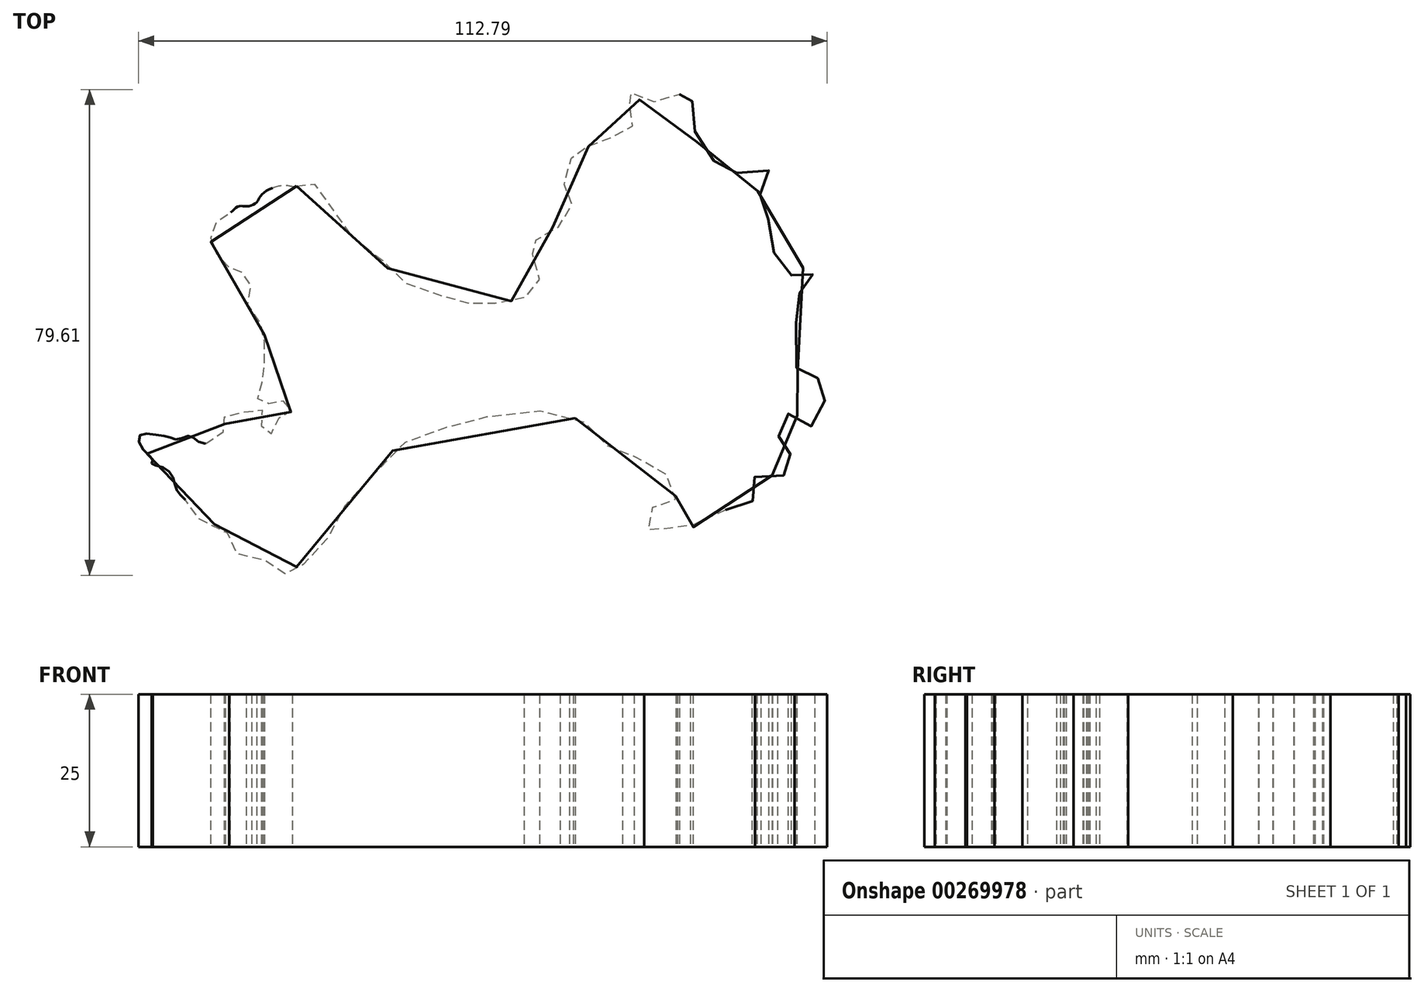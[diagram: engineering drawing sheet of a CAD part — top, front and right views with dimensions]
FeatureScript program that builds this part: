
annotation { "Feature Type Name" : "Feature", "Feature Type Description" : "" }
export const myFeature = defineFeature(function(context is Context, id is Id, definition is map)
    precondition{}
    {
        {
            var Q0;
            Q0=qCreatedBy(makeId("Top.planeOp"),FACE);
            var sketch = newSketch(context, id + "F0", { "sketchPlane" : qUnion([Q0])});
            skFitSpline(sketch, "E0", {"points": [v(-28.5, 30.47) * mm, v(-27.34, 31.77) * mm, v(-26.03, 31.34) * mm, v(-24.59, 29.31) * mm, v(-22.42, 26.42) * mm, v(-21.26, 23.82) * mm, v(-18.08, 21.36) * mm, v(-14.47, 18.33) * mm, v(-12.59, 15.72) * mm, v(-9.26, 14.13) * mm, v(-4.78, 12.54) * mm, v(-2.18, 11.38) * mm, v(0, 11.24) * mm, v(1.73, 10.52) * mm, v(4.33, 11.38) * mm, v(7.22, 11.67) * mm, v(9.68, 12.83) * mm, v(10.4, 14.28) * mm, v(11.27, 15.14) * mm, v(11.13, 16.88) * mm, v(10.4, 19.05) * mm, v(8.81, 21.36) * mm, v(10.55, 21.5) * mm, v(12.14, 23.53) * mm, v(14.45, 23.82) * mm, v(16.48, 25.55) * mm, v(16.62, 27.43) * mm, v(14.74, 29.46) * mm, v(15.18, 30.62) * mm, v(17.06, 32.06) * mm, v(16.33, 35.53) * mm, v(16.33, 36.4) * mm, v(18.65, 36.83) * mm, v(20.96, 37.41) * mm, v(22.84, 38.28) * mm, v(24.72, 39.44) * mm, v(26.3, 39.87) * mm, v(26.74, 41.75) * mm, v(26.74, 43.2) * mm, v(25.44, 44.79) * mm, v(25, 46.23) * mm, v(26.89, 45.36) * mm, v(28.62, 44.06) * mm, v(30.21, 44.35) * mm, v(32.67, 44.79) * mm, v(34.26, 45.5) * mm, v(33.97, 43.77) * mm, v(35.42, 43.77) * mm, v(36.43, 44.35) * mm, v(36, 41.75) * mm, v(36.58, 40.16) * mm, v(37.88, 35.39) * mm, v(39.47, 34.66) * mm, v(41.2, 33.94) * mm, v(42.8, 32.06) * mm, v(43.95, 32.93) * mm, v(46.26, 33.07) * mm, v(48.87, 33.07) * mm, v(47.7, 31.63) * mm, v(46.99, 29.9) * mm, v(47.57, 28.74) * mm, v(46.84, 27) * mm, v(48.43, 25.41) * mm, v(49.44, 23.24) * mm, v(49.44, 20.5) * mm, v(50.46, 18.18) * mm, v(51.47, 16.73) * mm, v(52.63, 15.87) * mm, v(54.36, 17.02) * mm, v(55.52, 17.02) * mm, v(56.24, 15.58) * mm, v(56.39, 14.57) * mm, v(55.23, 13.84) * mm, v(53.35, 12.25) * mm, v(53.06, 10.23) * mm, v(53.35, 8.06) * mm, v(53.5, 5.02) * mm, v(53.78, 0) * mm, v(54.94, 0) * mm, v(55.23, 0) * mm, v(56.96, -1.05) * mm, v(57.83, -1.34) * mm, v(58.4, -2.79) * mm, v(57.98, -5.1) * mm, v(57.69, -6.7) * mm, v(56.24, -8.86) * mm, v(54.8, -8.28) * mm, v(54.07, -7.41) * mm, v(52.2, -6.83) * mm, v(51.04, -7.41) * mm, v(50.31, -9.3) * mm, v(50.6, -10.74) * mm, v(51.32, -11.46) * mm, v(52.2, -11.9) * mm, v(52.48, -13.34) * mm, v(52.05, -14.35) * mm, v(53.06, -14.93) * mm, v(50.6, -17.25) * mm, v(48.58, -16.52) * mm, v(46.84, -16.96) * mm, v(46.12, -18.11) * mm, v(46.55, -19.41) * mm, v(46.4, -20.86) * mm, v(44.96, -21.87) * mm, v(43.08, -21.73) * mm, v(40.91, -23.17) * mm, v(36.86, -24.33) * mm, v(36.29, -26.21) * mm, v(34.12, -25.92) * mm, v(31.23, -25.78) * mm, v(30.07, -26.64) * mm, v(28.77, -25.05) * mm, v(28.62, -23.17) * mm, v(30.07, -22.16) * mm, v(32.24, -22.3) * mm, v(33.54, -21) * mm, v(33.54, -19.85) * mm, v(32.53, -17.54) * mm, v(30.94, -15.66) * mm, v(27.32, -14.06) * mm, v(24.43, -12.76) * mm, v(22.55, -12.18) * mm, v(21.1, -10.02) * mm, v(17.78, -7.85) * mm, v(12, -6.4) * mm, v(3.32, -7.41) * mm, v(0, -7.41) * mm, v(-6.51, -10.3) * mm, v(-10.85, -11.6) * mm, v(-15.2, -15.66) * mm, v(-17.5, -19.41) * mm, v(-21.7, -22.89) * mm, v(-22.7, -25.34) * mm, v(-25.75, -31.27) * mm, v(-27.48, -31.56) * mm, v(-28.2, -31.56) * mm, v(-29.5, -33.3) * mm, v(-31.24, -32.43) * mm, v(-32.4, -31.85) * mm, v(-33.55, -30.98) * mm, v(-36.01, -29.68) * mm, v(-38.18, -29.83) * mm, v(-39.48, -28.52) * mm, v(-39.48, -26.93) * mm, v(-40.93, -25.63) * mm, v(-43.82, -24.19) * mm, v(-45.56, -23.75) * mm, v(-45.99, -22.02) * mm, v(-47.44, -20.28) * mm, v(-48.3, -18.98) * mm, v(-48.88, -16.96) * mm, v(-50.76, -15.51) * mm, v(-52.2, -15.08) * mm, v(-52.06, -14.35) * mm, v(-53.5, -12.9) * mm, v(-54.23, -10.45) * mm, v(-51.48, -10.3) * mm, v(-49.17, -10.74) * mm, v(-47.87, -11.03) * mm, v(-45.99, -10.45) * mm, v(-44.54, -11.46) * mm, v(-41.94, -11.32) * mm, v(-40.2, -8.86) * mm, v(-40.35, -7.56) * mm, v(-39.05, -6.55) * mm, v(-35.43, -6.7) * mm, v(-33.99, -6.26) * mm, v(-34.28, -8.43) * mm, v(-33.26, -10.6) * mm, v(-31.82, -8.43) * mm, v(-31.24, -7.41) * mm, v(-29.8, -6.83) * mm, v(-29.22, -5.97) * mm, v(-30.23, -4.96) * mm, v(-31.67, -4.67) * mm, v(-33.4, -5.24) * mm, v(-35, -4.67) * mm, v(-34.28, -3.65) * mm, v(-34.13, -1.34) * mm, v(-33.84, 0) * mm, v(-33.84, 4.15) * mm, v(-33.84, 6.9) * mm, v(-35.43, 9.36) * mm, v(-36.74, 12.4) * mm, v(-35.87, 14.71) * mm, v(-37.17, 16.16) * mm, v(-38.76, 17.02) * mm, v(-40.06, 17.46) * mm, v(-41.5, 19.34) * mm, v(-42.52, 21.07) * mm, v(-42.23, 23.39) * mm, v(-41.36, 24.83) * mm, v(-39.63, 25.84) * mm, v(-38.04, 27.15) * mm, v(-36.6, 27.15) * mm, v(-35, 27.87) * mm, v(-34.13, 29.17) * mm, v(-30.37, 30.62) * mm, v(-28.5, 30.47) * mm]});
            skSolve(sketch);
        }
        {
            var Q0;
            Q0 = qSketchRegion(id + "F0", true);
            extrude(context, id + "F1", {"entities" : qUnion([Q0]), "depth" : 25 * mm});
        }
        {
            var Q0;
            Q0=makeQuery(id+"F1.opExtrude","CAP_FACE",FACE,{"disambiguationData":[OSD([sQuery(id+"F0.wireOp",EDGE,"E0")])],"isStart":false});
            cPlane(context, id + "F2", {"entities" : qUnion([Q0]), "cplaneType" : CPlaneType.OFFSET, "offset" : 0 * mm, "width" : 150 * mm, "height" : 150 * mm});
        }
    });
